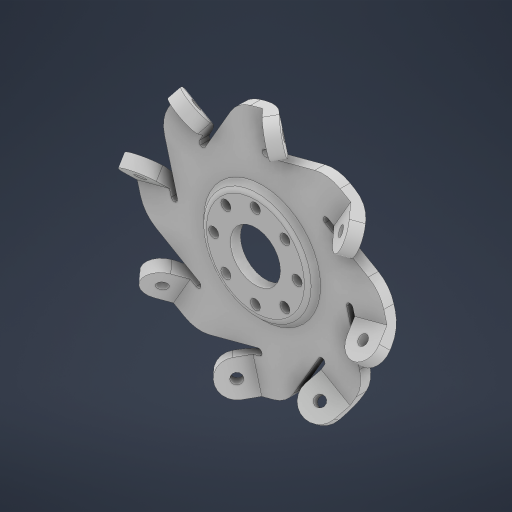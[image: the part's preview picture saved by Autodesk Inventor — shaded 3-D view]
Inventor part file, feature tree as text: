
AUTODESK INVENTOR PART (.ipt)
format: ipt  version: 2023 (Build 270158000, 158)  size: 479,232 bytes
history: native  units: mm
features: extrude x6, fillet x4, sketch x3, pattern_circular x2, chamfer x2, plane x1
ambient origin geometry x8: Origin, YZ Plane, XZ Plane, XY Plane, X Axis, Y Axis, Z Axis, Center Point
bodies: Solid1 (feature_tree)
feature tree (18):
  sketch  "Sketch1"  dims[d0=15.0mm d1=50.0mm]
  extrude  "Extrusion1"  Depth=15.0mm
  plane  "Work Plane1"
  extrude  "Extrusion2"  Depth=3.0mm
  fillet  "Fillet1"  Radius=3.0mm
  extrude  "Extrusion3"  Depth=2.0mm
  pattern_circular  "Circular Pattern1"  [2 undecoded]
  fillet  "Fillet2"  [1 undecoded]
  fillet  "Fillet3"  Radius=10.0mm
  pattern_circular  "Circular Pattern2"  [2 undecoded]
  extrude  "Extrusion4"  Depth=2.0mm TaperAngle=360.0deg
  extrude  "Extrusion5"  Depth=3.0mm TaperAngle=0.0deg
  extrude  "Extrusion6"  TaperAngle=135.0deg  [1 undecoded]
  chamfer  "Chamfer1"  Distance=10.0mm
  chamfer  "Chamfer2"  Distance=5.0mm
  fillet  "Fillet4"  Radius=3.0mm
  sketch  "Sketch2"  dims[d3=3.0mm d4=3.0mm d5=3.0mm]
  sketch  "Sketch3"  dims[d6=3.0mm d8=2.0mm d13=5.0mm d14=30.0deg d15=10.0mm d16=10.0mm d17=80.0mm d19=360.0deg d21=3.0mm d22=0.0mm d23=135.0deg d24=10.0mm d25=0.0mm d26=5.0mm d27=3.0mm d28=10.0mm d29=0.0mm d30=80.0mm d31=360.0deg d33=10.0mm d34=1.0mm d35=80.0mm d36=360.0deg d38=3.0mm d39=3.0mm d40=3.0mm d41=3.0mm d42=35.0mm d43=3.0mm d44=0.0mm d45=5.0mm d46=0.0mm d47=32.0mm d48=2.0mm d49=0.0mm d50=2.0mm d51=2.0mm d52=45.0deg d53=2.0mm d54=2.0mm d55=45.0deg d56=2.0mm]
note: 6 required parameter values undecoded (feature->parameter linkage not recoverable at this tier; creation-order binding heuristic only, values carry confidence <= 0.55)
